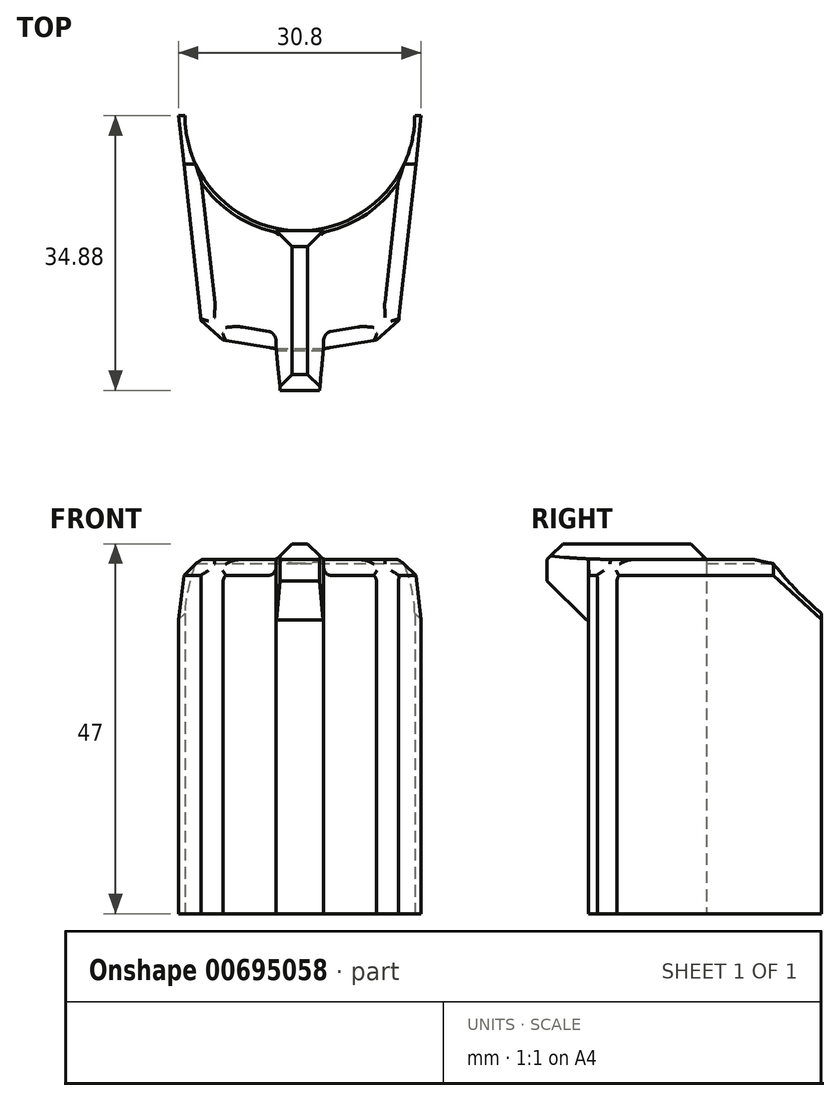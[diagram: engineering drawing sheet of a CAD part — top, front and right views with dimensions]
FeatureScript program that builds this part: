
annotation { "Feature Type Name" : "Feature", "Feature Type Description" : "" }
export const myFeature = defineFeature(function(context is Context, id is Id, definition is map)
    precondition{}
    {
        {
            var Q0;
            Q0=qCreatedBy(makeId("Top.planeOp"),FACE);
            var sketch = newSketch(context, id + "F0", { "sketchPlane" : qUnion([Q0])});
            skCircle(sketch, "E0", {"center": v(0, 0) * mm, "radius": 17.5 * mm, "construction": true});
            skCircle(sketch, "E1", {"center": v(0, -22.1) * mm, "radius": 7.5 * mm, "construction": true});
            skCircle(sketch, "E2.cCircle", {"center": v(0, 0) * mm, "radius": 3.5 * mm, "construction": true});
            skLineSegment(sketch, "E2.0", {"start": v(6.06, -3.5) * mm, "end": v(-6.06, -3.5) * mm, "construction": true});
            skLineSegment(sketch, "E2.1", {"start": v(-6.06, -3.5) * mm, "end": v(0, 7) * mm, "construction": true});
            skLineSegment(sketch, "E2.2", {"start": v(0, 7) * mm, "end": v(6.06, -3.5) * mm, "construction": true});
            skPoint(sketch, "E2.0.midPoint", {"position": v(0, -3.5) * mm});
            skCircle(sketch, "E3", {"center": v(0, 7) * mm, "radius": 6 * mm, "construction": true});
            skCircle(sketch, "E4", {"center": v(6.06, -3.5) * mm, "radius": 6 * mm, "construction": true});
            skCircle(sketch, "E5", {"center": v(-6.06, -3.5) * mm, "radius": 6 * mm, "construction": true});
            skCircle(sketch, "E6", {"center": v(0, 0) * mm, "radius": 13 * mm, "construction": true});
            skCircle(sketch, "E7.0", {"center": v(0, 0) * mm, "radius": 13.8 * mm, "construction": true});
            skCircle(sketch, "E8.0", {"center": v(0, 7) * mm, "radius": 5.2 * mm, "construction": true});
            skCircle(sketch, "E9.0", {"center": v(6.06, -3.5) * mm, "radius": 5.2 * mm, "construction": true});
            skCircle(sketch, "E10.0", {"center": v(-6.06, -3.5) * mm, "radius": 5.2 * mm, "construction": true});
            skLineSegment(sketch, "E11", {"start": v(30.84, -29.6) * mm, "end": v(-27.41, -29.6) * mm, "construction": true});
            skLineSegment(sketch, "E12", {"start": v(-15.4, 0) * mm, "end": v(-15.4, -32.5) * mm, "construction": true});
            skLineSegment(sketch, "E13", {"start": v(15.4, 0) * mm, "end": v(15.4, -32.5) * mm, "construction": true});
            skLineSegment(sketch, "E14.0", {"start": v(-14.6, 0) * mm, "end": v(-14.6, -32.5) * mm, "construction": true});
            skLineSegment(sketch, "E15.0", {"start": v(14.6, 0) * mm, "end": v(14.6, -32.5) * mm, "construction": true});
            skCircle(sketch, "E16.0", {"center": v(0, 0) * mm, "radius": 14.6 * mm, "construction": true});
            skLineSegment(sketch, "E17.bottom", {"start": v(-3, -14.6) * mm, "end": v(3, -14.6) * mm});
            skLineSegment(sketch, "E17.top", {"start": v(-2.5, -34.88) * mm, "end": v(2.5, -34.88) * mm});
            skLineSegment(sketch, "E17.left", {"start": v(-3, -14.6) * mm, "end": v(-3, -29.6) * mm});
            skLineSegment(sketch, "E17.right", {"start": v(3, -14.6) * mm, "end": v(3, -29.6) * mm});
            skLineSegment(sketch, "E18", {"start": v(-15.4, 0) * mm, "end": v(-12.56, -26) * mm});
            skLineSegment(sketch, "E19", {"start": v(-12.56, -26) * mm, "end": v(-9.74, -28.47) * mm});
            skLineSegment(sketch, "E20", {"start": v(-9.74, -28.47) * mm, "end": v(-3, -29.6) * mm});
            skLineSegment(sketch, "E21", {"start": v(-15.4, 0) * mm, "end": v(-14.6, 0) * mm});
            skArc(sketch, "E22", {"start": v(-14.6, 0) * mm, "mid": v(0, -14.6) * mm, "end": v(14.6, 0) * mm});
            skLineSegment(sketch, "E23.MirrorCS", {"start": v(9.74, -28.47) * mm, "end": v(3, -29.6) * mm});
            skLineSegment(sketch, "E24.MirrorCS", {"start": v(15.4, 0) * mm, "end": v(12.56, -26) * mm});
            skLineSegment(sketch, "E25.MirrorCS", {"start": v(12.56, -26) * mm, "end": v(9.74, -28.47) * mm});
            skLineSegment(sketch, "E26", {"start": v(15.4, 0) * mm, "end": v(14.6, 0) * mm});
            skLineSegment(sketch, "E27", {"start": v(-2.5, -34.88) * mm, "end": v(-3, -29.6) * mm});
            skLineSegment(sketch, "E28", {"start": v(2.5, -34.88) * mm, "end": v(3, -29.6) * mm});
            skLineSegment(sketch, "E29", {"start": v(-3, -29.6) * mm, "end": v(3, -29.6) * mm});
            skSolve(sketch);
        }
        {
            var Q0;
            {var subQ4=sQuery(id+"F0.wireOp",EDGE,"E17.right");Q0=makeQuery(id+"F0.imprint","IMPRINT",FACE,{"disambiguationData":[TD([[makeQuery(id+"F0.imprint","IMPRINT",EDGE,{"derivedFrom":subQ4}),1.0]])]});}
            var Q1;
            {var subQ1=sQuery(id+"F0.wireOp",EDGE,"E17.left");Q1=makeQuery(id+"F0.imprint","IMPRINT",FACE,{"disambiguationData":[TD([[makeQuery(id+"F0.imprint","IMPRINT",EDGE,{"derivedFrom":subQ1}),1.0]])]});}
            var Q2;
            {var subQ0=sQuery(id+"F0.wireOp",EDGE,"E17.left");Q2=makeQuery(id+"F0.imprint","IMPRINT",FACE,{"disambiguationData":[TD([[makeQuery(id+"F0.imprint","IMPRINT",EDGE,{"derivedFrom":subQ0}),-1.0]])]});}
            extrude(context, id + "F1", {"entities" : qUnion([Q0, Q1, Q2]), "depth" : 45 * mm, "offsetDistance" : 25 * mm});
        }
        {
            var Q0;
            Q0=makeQuery(id+"F0.imprint","IMPRINT",FACE,{"disambiguationData":[TD([[makeQuery(id+"F0.imprint","IMPRINT",EDGE,{"derivedFrom":sQuery(id+"F0.wireOp",EDGE,"E17.top")}),1.0]])]});
            var Q1;
            {var subQ1=sQuery(id+"F0.wireOp",EDGE,"E17.left");Q1=makeQuery(id+"F0.imprint","IMPRINT",FACE,{"disambiguationData":[TD([[makeQuery(id+"F0.imprint","IMPRINT",EDGE,{"derivedFrom":subQ1}),1.0]])]});}
            extrude(context, id + "F2", {"entities" : qUnion([Q0, Q1]), "operationType" : NewBodyOperationType.ADD, "depth" : 47 * mm, "offsetDistance" : 25 * mm, "hasSecondDirection" : true, "secondDirectionOppositeDirection" : false, "secondDirectionDepth" : 37.3 * mm});
        }
        {
            var Q0;
            Q0=makeQuery(id+"F1.opExtrude","CAP_EDGE",EDGE,{"disambiguationData":[OSD([sQuery(id+"F0.wireOp",EDGE,"E18")])],"isStart":false});
            var Q1;
            Q1=makeQuery(id+"F1.opExtrude","CAP_EDGE",EDGE,{"disambiguationData":[OSD([sQuery(id+"F0.wireOp",EDGE,"E24.MirrorCS")])],"isStart":false});
            var Q2;
            Q2=makeQuery(id+"F1.opExtrude","CAP_EDGE",EDGE,{"disambiguationData":[OSD([sQuery(id+"F0.wireOp",EDGE,"E20")])],"isStart":false});
            var Q3;
            Q3=makeQuery(id+"F1.opExtrude","CAP_EDGE",EDGE,{"disambiguationData":[OSD([sQuery(id+"F0.wireOp",EDGE,"E23.MirrorCS")])],"isStart":false});
            var Q4;
            Q4=makeQuery(id+"F1.opExtrude","CAP_EDGE",EDGE,{"disambiguationData":[OSD([sQuery(id+"F0.wireOp",EDGE,"E25.MirrorCS")])],"isStart":false});
            var Q5;
            Q5=makeQuery(id+"F1.opExtrude","CAP_EDGE",EDGE,{"disambiguationData":[OSD([sQuery(id+"F0.wireOp",EDGE,"E19")])],"isStart":false});
            chamfer(context, id + "F3", {"entities" : qUnion([Q0, Q1, Q2, Q3, Q4, Q5]), "width" : 2 * mm, "tangentPropagation" : true});
        }
        {
            var Q0;
            Q0=makeQuery(id+"F1.opExtrude","CAP_EDGE",EDGE,{"disambiguationData":[OSD([sQuery(id+"F0.wireOp",EDGE,"E22")])],"isStart":false});
            chamfer(context, id + "F4", {"entities" : qUnion([Q0]), "width" : 0.5 * mm, "tangentPropagation" : true});
        }
        {
            var Q0;
            Q0=makeQuery(id+"FCIBW1QCwEhE8w7_1.opChamfer","BLEND_FACE",FACE,{"disambiguationData":[OSD([sQuery(id+"F0.wireOp",EDGE,"E17.top")])]});
            var Q1;
            Q1=makeQuery(id+"F3.opChamfer","BLEND_FACE",FACE,{"disambiguationData":[OSD([sQuery(id+"F0.wireOp",EDGE,"E19")])]});
            var Q2;
            Q2=makeQuery(id+"F3.opChamfer","BLEND_FACE",FACE,{"disambiguationData":[OSD([sQuery(id+"F0.wireOp",EDGE,"E25.MirrorCS")])]});
            fillet(context, id + "F5", {"entities" : qUnion([Q0, Q1, Q2]), "radius" : 2 * mm, "tangentPropagation" : true, "allowEdgeOverflow" : false});
        }
        {
            var Q0;
            Q0=makeQuery(id+"F3.opChamfer","BLEND_EDGE",EDGE,{"blendedFrom":[makeQuery(id+"F1.opExtrude","CAP_EDGE",EDGE,{"disambiguationData":[OSD([sQuery(id+"F0.wireOp",EDGE,"E18")])],"isStart":false}),makeQuery(id+"F1.opExtrude","SWEPT_FACE",FACE,{"disambiguationData":[OSD([sQuery(id+"F0.wireOp",EDGE,"E21")])]})],"blendedInto":[makeQuery(id+"F1.opExtrude","SWEPT_FACE",FACE,{"disambiguationData":[OSD([sQuery(id+"F0.wireOp",EDGE,"E21")])]})]});
            var Q1;
            Q1=makeQuery(id+"F3.opChamfer","BLEND_EDGE",EDGE,{"blendedFrom":[makeQuery(id+"F1.opExtrude","CAP_EDGE",EDGE,{"disambiguationData":[OSD([sQuery(id+"F0.wireOp",EDGE,"E24.MirrorCS")])],"isStart":false}),makeQuery(id+"F1.opExtrude","SWEPT_FACE",FACE,{"disambiguationData":[OSD([sQuery(id+"F0.wireOp",EDGE,"E26")])]})],"blendedInto":[makeQuery(id+"F1.opExtrude","SWEPT_FACE",FACE,{"disambiguationData":[OSD([sQuery(id+"F0.wireOp",EDGE,"E26")])]})]});
            chamfer(context, id + "F6", {"entities" : qUnion([Q0, Q1]), "chamferType" : ChamferType.OFFSET_ANGLE, "width" : 4 * mm, "oppositeDirection" : false, "angle" : 60 * degree, "tangentPropagation" : true});
        }
        {
            var Q0;
            Q0=makeQuery(id+"F2.opExtrude","CAP_EDGE",EDGE,{"disambiguationData":[OSD([sQuery(id+"F0.wireOp",EDGE,"E17.bottom")])],"isStart":false});
            var Q1;
            Q1=makeQuery(id+"F2.opExtrude","CAP_EDGE",EDGE,{"disambiguationData":[OSD([sQuery(id+"F0.wireOp",EDGE,"E17.left")])],"isStart":false});
            var Q2;
            Q2=makeQuery(id+"F2.opExtrude","CAP_EDGE",EDGE,{"disambiguationData":[OSD([sQuery(id+"F0.wireOp",EDGE,"E17.right")])],"isStart":false});
            var Q3;
            Q3=makeQuery(id+"F2.opExtrude","CAP_EDGE",EDGE,{"disambiguationData":[OSD([sQuery(id+"F0.wireOp",EDGE,"E17.top")])],"isStart":false});
            chamfer(context, id + "F7", {"entities" : qUnion([Q0, Q1, Q2, Q3]), "width" : 2 * mm, "tangentPropagation" : true});
        }
        {
            var Q0;
            Q0=makeQuery(id+"F2.opExtrude","CAP_EDGE",EDGE,{"disambiguationData":[OSD([sQuery(id+"F0.wireOp",EDGE,"E17.top")])],"isStart":true});
            chamfer(context, id + "F8", {"entities" : qUnion([Q0]), "width" : 5 * mm, "tangentPropagation" : true});
        }
        {
            var Q0;
            Q0=makeQuery(id+"F3.opChamfer","BLEND_EDGE",EDGE,{"blendedFrom":[makeQuery(id+"F1.opExtrude","CAP_EDGE",EDGE,{"disambiguationData":[OSD([sQuery(id+"F0.wireOp",EDGE,"E20")])],"isStart":false}),makeQuery(id+"F2.opExtrude","SWEPT_FACE",FACE,{"disambiguationData":[OSD([sQuery(id+"F0.wireOp",EDGE,"E17.left")])]})],"blendedInto":[makeQuery(id+"F2.opExtrude","SWEPT_FACE",FACE,{"disambiguationData":[OSD([sQuery(id+"F0.wireOp",EDGE,"E17.left")])]})]});
            var Q1;
            Q1=makeQuery(id+"F3.opChamfer","BLEND_EDGE",EDGE,{"blendedFrom":[makeQuery(id+"F1.opExtrude","CAP_EDGE",EDGE,{"disambiguationData":[OSD([sQuery(id+"F0.wireOp",EDGE,"E23.MirrorCS")])],"isStart":false}),makeQuery(id+"F2.opExtrude","SWEPT_FACE",FACE,{"disambiguationData":[OSD([sQuery(id+"F0.wireOp",EDGE,"E17.right")])]})],"blendedInto":[makeQuery(id+"F2.opExtrude","SWEPT_FACE",FACE,{"disambiguationData":[OSD([sQuery(id+"F0.wireOp",EDGE,"E17.right")])]})]});
            var Q2;
            {var subQ0=sQuery(id+"F0.wireOp",EDGE,"E20");var subQ1=sQuery(id+"F0.wireOp",EDGE,"E19");var subQ2=sQuery(id+"F0.wireOp",EDGE,"E22");var subQ3=sQuery(id+"F0.wireOp",EDGE,"E21");var subQ4=sQuery(id+"F0.wireOp",EDGE,"E18");var subQ5=makeQuery(id+"F1.opExtrude","CAP_FACE",FACE,{"disambiguationData":[OSD([subQ4,subQ1,subQ0,subQ3,subQ2,sQuery(id+"F0.wireOp",EDGE,"E23.MirrorCS"),sQuery(id+"F0.wireOp",EDGE,"E24.MirrorCS"),sQuery(id+"F0.wireOp",EDGE,"E25.MirrorCS"),sQuery(id+"F0.wireOp",EDGE,"E26"),sQuery(id+"F0.wireOp",EDGE,"E29")])],"isStart":false});var subQ6=sQuery(id+"F0.wireOp",EDGE,"E17.left");Q2=makeQuery(id+"F7.opChamfer","BLEND_EDGE",EDGE,{"blendedFrom":[makeQuery(id+"F2.opExtrude","CAP_EDGE",EDGE,{"disambiguationData":[OSD([subQ6])],"isStart":false}),makeQuery(id+"F2.boolean.opBoolean","SPLIT",FACE,{"disambiguationData":[TD([makeQuery(id+"F1.opExtrude","SWEPT_FACE",FACE,{"disambiguationData":[OSD([subQ4])]})])],"derivedFrom":subQ5})],"blendedInto":[makeQuery(id+"F2.boolean.opBoolean","SPLIT",FACE,{"disambiguationData":[TD([makeQuery(id+"F1.opExtrude","SWEPT_FACE",FACE,{"disambiguationData":[OSD([subQ4])]})])],"derivedFrom":subQ5})]});}
            var Q3;
            {var subQ0=sQuery(id+"F0.wireOp",EDGE,"E24.MirrorCS");var subQ1=sQuery(id+"F0.wireOp",EDGE,"E22");var subQ2=sQuery(id+"F0.wireOp",EDGE,"E23.MirrorCS");var subQ3=sQuery(id+"F0.wireOp",EDGE,"E26");var subQ4=sQuery(id+"F0.wireOp",EDGE,"E25.MirrorCS");var subQ5=makeQuery(id+"F1.opExtrude","CAP_FACE",FACE,{"disambiguationData":[OSD([sQuery(id+"F0.wireOp",EDGE,"E18"),sQuery(id+"F0.wireOp",EDGE,"E19"),sQuery(id+"F0.wireOp",EDGE,"E20"),sQuery(id+"F0.wireOp",EDGE,"E21"),subQ1,subQ2,subQ0,subQ4,subQ3,sQuery(id+"F0.wireOp",EDGE,"E29")])],"isStart":false});var subQ6=sQuery(id+"F0.wireOp",EDGE,"E17.right");Q3=makeQuery(id+"F7.opChamfer","BLEND_EDGE",EDGE,{"blendedFrom":[makeQuery(id+"F2.opExtrude","CAP_EDGE",EDGE,{"disambiguationData":[OSD([subQ6])],"isStart":false}),makeQuery(id+"F2.boolean.opBoolean","SPLIT",FACE,{"disambiguationData":[TD([makeQuery(id+"F1.opExtrude","SWEPT_FACE",FACE,{"disambiguationData":[OSD([subQ2])]})])],"derivedFrom":subQ5})],"blendedInto":[makeQuery(id+"F2.boolean.opBoolean","SPLIT",FACE,{"disambiguationData":[TD([makeQuery(id+"F1.opExtrude","SWEPT_FACE",FACE,{"disambiguationData":[OSD([subQ2])]})])],"derivedFrom":subQ5})]});}
            fillet(context, id + "F9", {"entities" : qUnion([Q0, Q1, Q2, Q3]), "radius" : 1 * mm, "tangentPropagation" : true, "allowEdgeOverflow" : false});
        }
    });
